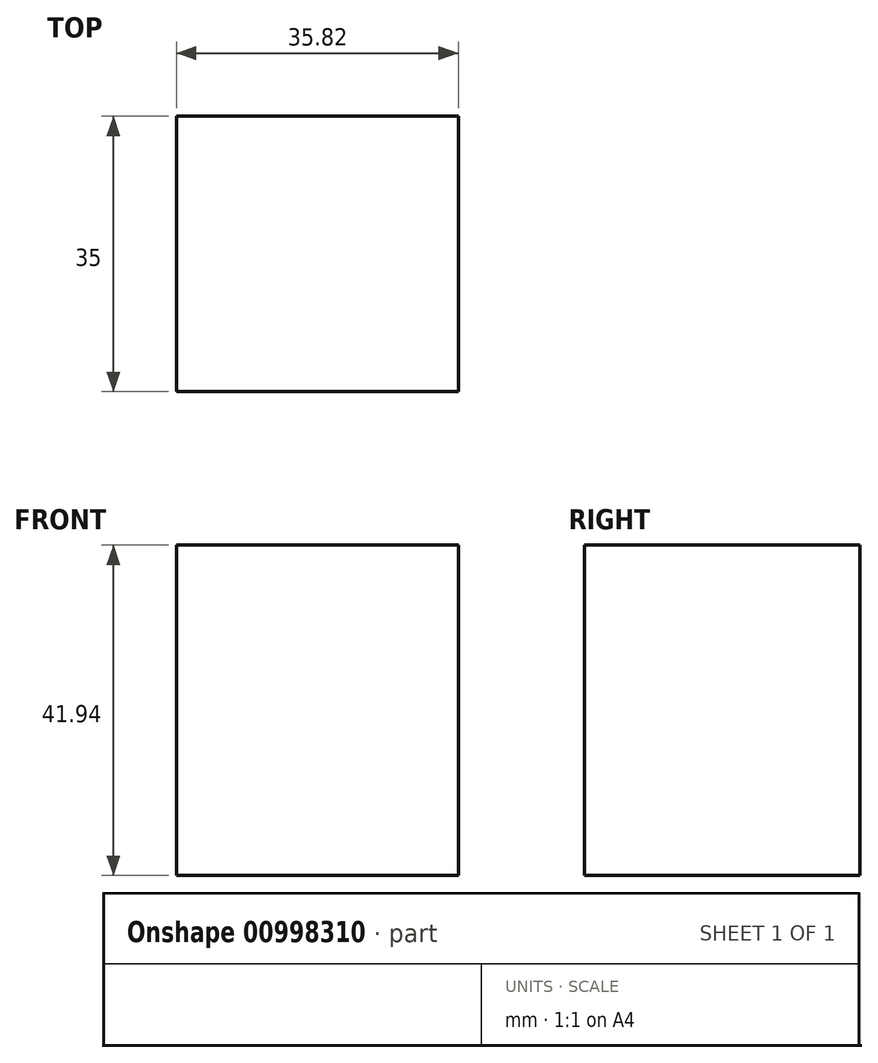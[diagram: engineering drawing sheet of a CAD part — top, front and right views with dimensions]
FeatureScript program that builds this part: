
annotation { "Feature Type Name" : "Feature", "Feature Type Description" : "" }
export const myFeature = defineFeature(function(context is Context, id is Id, definition is map)
    precondition{}
    {
        {
            var Q0;
            Q0=qCreatedBy(makeId("Front.planeOp"),FACE);
            var sketch = newSketch(context, id + "F0", { "sketchPlane" : qUnion([Q0])});
            skCircle(sketch, "E0", {"center": v(0, 0) * mm, "radius": 14.5 * mm, "construction": true});
            skLineSegment(sketch, "E1.bottom", {"start": v(-17.91, 20.97) * mm, "end": v(17.91, 20.97) * mm});
            skLineSegment(sketch, "E1.top", {"start": v(-17.91, -20.97) * mm, "end": v(17.91, -20.97) * mm});
            skLineSegment(sketch, "E1.left", {"start": v(-17.91, 20.97) * mm, "end": v(-17.91, -20.97) * mm});
            skLineSegment(sketch, "E1.right", {"start": v(17.91, 20.97) * mm, "end": v(17.91, -20.97) * mm});
            skLineSegment(sketch, "E2", {"start": v(0, 37.74) * mm, "end": v(0, -36.87) * mm, "construction": true});
            skLineSegment(sketch, "E3", {"start": v(-30.83, 0) * mm, "end": v(40.08, 0) * mm, "construction": true});
            skSolve(sketch);
        }
        {
            var Q0;
            Q0=makeQuery(id+"F0.imprint","IMPRINT",FACE,{"disambiguationData":[TD([[makeQuery(id+"F0.imprint","IMPRINT",EDGE,{"derivedFrom":sQuery(id+"F0.wireOp",EDGE,"E1.bottom")}),-1.0]])]});
            extrude(context, id + "F1", {"entities" : qUnion([Q0]), "endBound" : BoundingType.SYMMETRIC, "depth" : 35 * mm, "offsetDistance" : 25 * mm});
        }
    });
